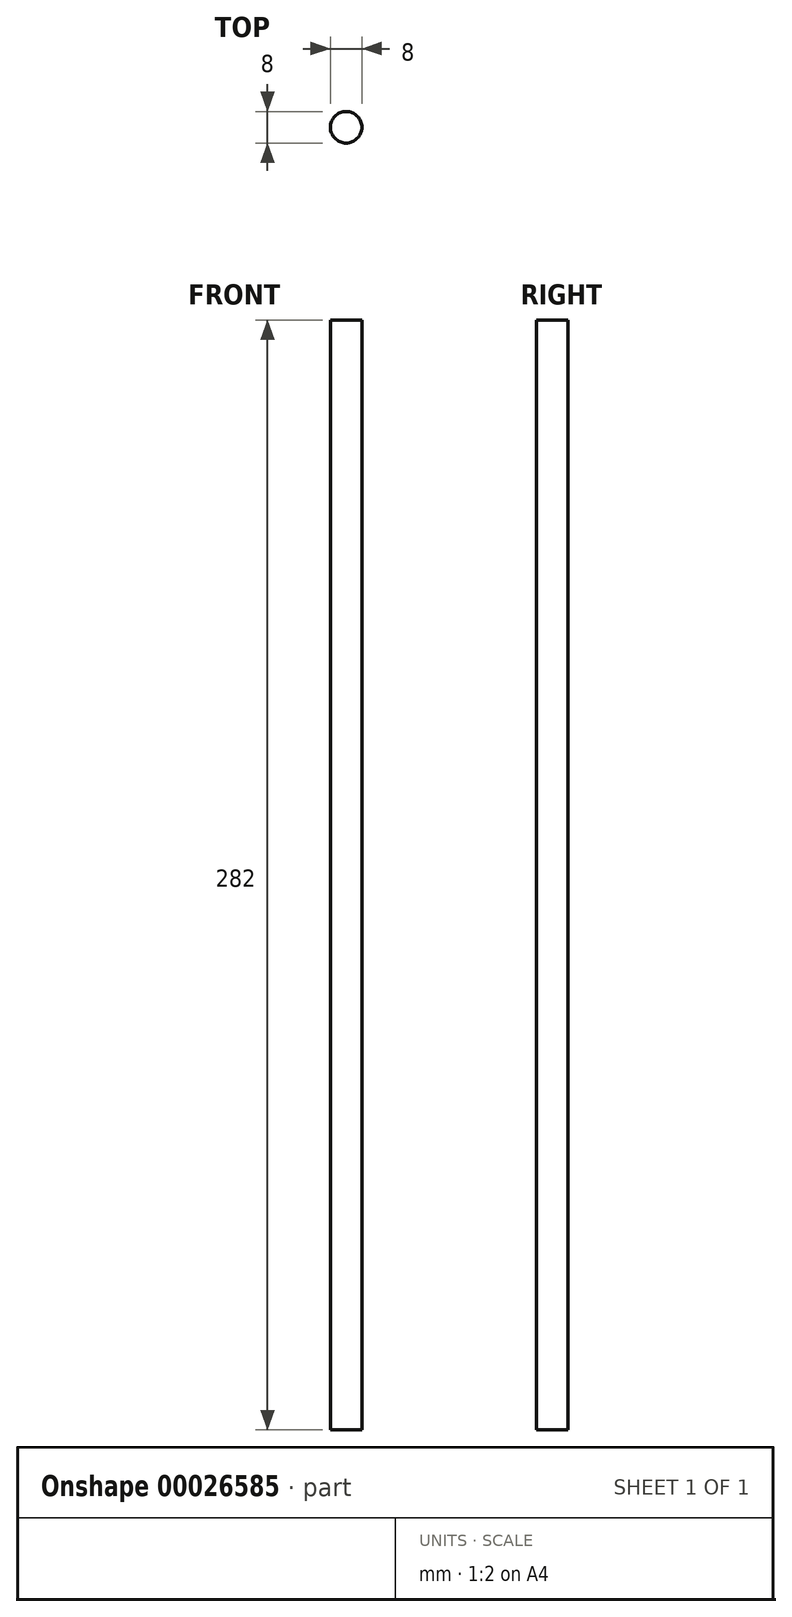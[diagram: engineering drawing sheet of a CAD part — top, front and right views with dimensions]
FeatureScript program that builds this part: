
annotation { "Feature Type Name" : "Feature", "Feature Type Description" : "" }
export const myFeature = defineFeature(function(context is Context, id is Id, definition is map)
    precondition{}
    {
        {
            var Q0;
            Q0=qCreatedBy(makeId("Top.planeOp"),FACE);
            var sketch = newSketch(context, id + "F0", { "sketchPlane" : qUnion([Q0])});
            skCircle(sketch, "E0", {"center": v(0, 0) * mm, "radius": 4 * mm});
            skSolve(sketch);
        }
        {
            var Q0;
            Q0=qSketchRegion(id+"F0",true);
            extrude(context, id + "F1", {"entities" : qUnion([Q0]), "depth" : 282 * mm});
        }
    });
